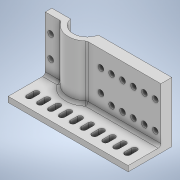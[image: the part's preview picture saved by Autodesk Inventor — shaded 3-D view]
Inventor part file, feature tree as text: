
AUTODESK INVENTOR PART (.ipt)
format: ipt  version: 2022 (Build 260153000, 153)  size: 261,120 bytes
history: native  units: in
note: dims shown in document units (in); Inventor stores cm internally (conversion verified against a paired STEP export)
features: sketch x5, extrude x3, hole x2, fillet x2
ambient origin geometry x8: Origin, YZ Plane, XZ Plane, XY Plane, X Axis, Y Axis, Z Axis, Center Point
bodies: Solid1 (feature_tree)
feature tree (12):
  extrude  "Extrusion1"  Depth=5.5in
  extrude  "Extrusion2"  Depth=0.25in
  hole  "Hole1"  [1 undecoded]
  fillet  "Fillet1"  Radius=1.75in
  extrude  "Extrusion3"  Depth=0.5in
  hole  "Hole2"  [1 undecoded]
  fillet  "Fillet2"  Radius=0.25in
  sketch  "Sketch1"  dims[d0=2.0in d1=5.5in]
  sketch  "Sketch2"  dims[d19=0.25in d20=0.0in d22=1.3in]
  sketch  "Sketch3"  dims[d23=0.125in d24=1.5in d25=1.75in]
  sketch  "Sketch6"  dims[d26=0.3in d27=0.5in]
  sketch  "Sketch7"  dims[d28=2.5in d29=0.0in d30=2.75in d31=0.25in d32=0.75in d33=0.75in d34=0.266in d35=0.75in d36=0.375in d37=0.25in d38=0.5635in d39=1.0in d40=0.8108in d41=0.325in d42=0.25in d43=0.5in d44=0.325in d45=0.25in d47=0.125in d49=1.3in d50=1.0in d51=0.0in d52=0.25in d53=2.75in d54=0.75in d55=0.75in d56=0.266in d57=0.75in d58=0.375in d59=0.25in d60=0.5635in d61=1.0in d62=0.8108in d63=1.0in d64=1.25in d65=0.5in d66=0.5in d67=0.5in d68=0.5in d69=0.625in d70=1.9685in d72=1.0in d73=0.3937in d75=1.0in d77=0.125in]
note: 2 required parameter values undecoded (feature->parameter linkage not recoverable at this tier; creation-order binding heuristic only, values carry confidence <= 0.55)
